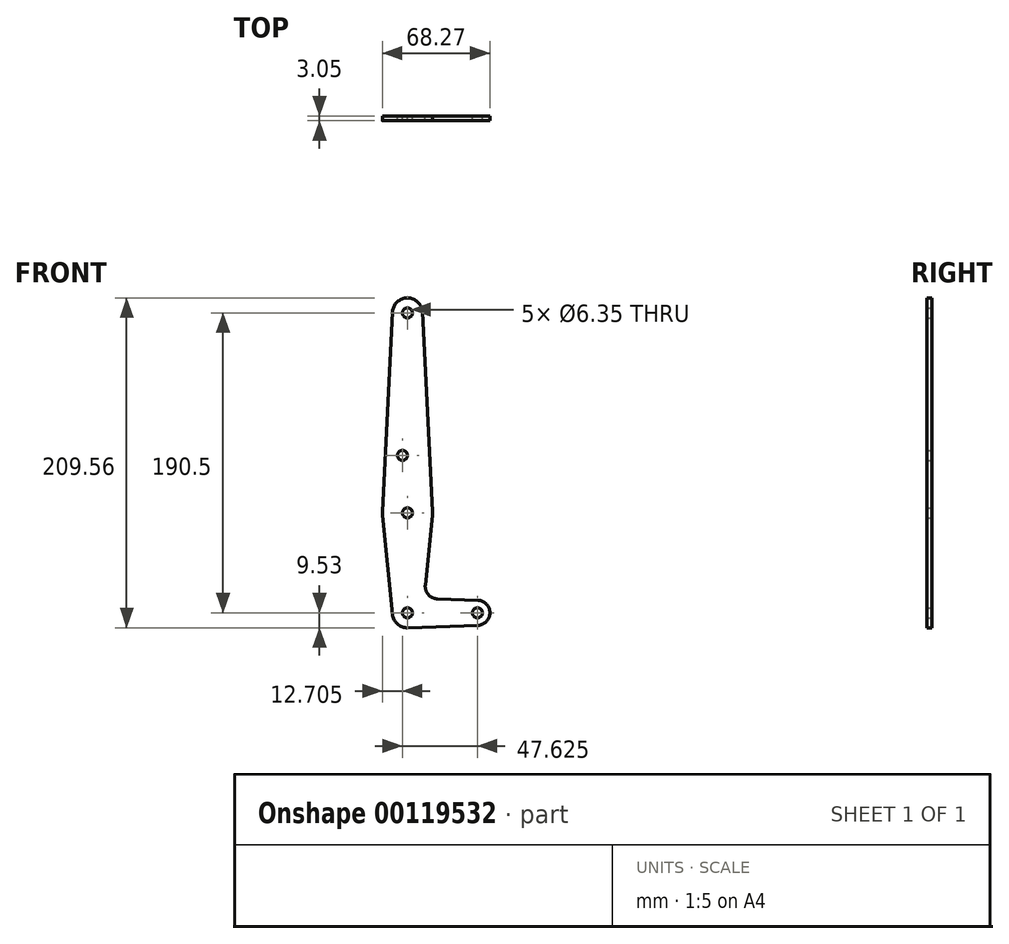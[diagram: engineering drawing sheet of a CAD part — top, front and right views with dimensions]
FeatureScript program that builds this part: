
annotation { "Feature Type Name" : "Feature", "Feature Type Description" : "" }
export const myFeature = defineFeature(function(context is Context, id is Id, definition is map)
    precondition{}
    {
        {
            var Q0;
            Q0=qCreatedBy(makeId("Front.planeOp"),FACE);
            var sketch = newSketch(context, id + "F0", { "sketchPlane" : qUnion([Q0])});
            skCircle(sketch, "E0", {"center": v(0, 0) * mm, "radius": 15.88 * mm});
            skCircle(sketch, "E1", {"center": v(0, 127) * mm, "radius": 9.53 * mm});
            skCircle(sketch, "E2", {"center": v(0, -63.5) * mm, "radius": 9.53 * mm});
            skCircle(sketch, "E3", {"center": v(44.45, -63.5) * mm, "radius": 7.94 * mm});
            skLineSegment(sketch, "E4", {"start": v(0, 127) * mm, "end": v(0, -63.5) * mm, "construction": true});
            skLineSegment(sketch, "E5", {"start": v(0, -63.5) * mm, "end": v(44.45, -63.5) * mm, "construction": true});
            skLineSegment(sketch, "E6", {"start": v(-15.8, -1.59) * mm, "end": v(-9.48, -64.45) * mm});
            skLineSegment(sketch, "E7", {"start": v(15.8, -1.59) * mm, "end": v(11.34, -45.9) * mm});
            skLineSegment(sketch, "E8", {"start": v(-9.51, 127.48) * mm, "end": v(-15.86, 0.8) * mm});
            skLineSegment(sketch, "E9", {"start": v(9.51, 127.48) * mm, "end": v(15.86, 0.8) * mm});
            skLineSegment(sketch, "E10", {"start": v(18.97, -54.65) * mm, "end": v(44.73, -55.57) * mm});
            skLineSegment(sketch, "E11", {"start": v(0.34, -73.02) * mm, "end": v(44.73, -71.43) * mm});
            skCircle(sketch, "E12", {"center": v(0, 127) * mm, "radius": 3.18 * mm});
            skCircle(sketch, "E13", {"center": v(0, 0) * mm, "radius": 3.18 * mm});
            skCircle(sketch, "E14", {"center": v(0, -63.5) * mm, "radius": 3.18 * mm});
            skCircle(sketch, "E15", {"center": v(44.45, -63.5) * mm, "radius": 3.18 * mm});
            skCircle(sketch, "E16", {"center": v(-3.17, 36.53) * mm, "radius": 3.18 * mm});
            skArc(sketch, "E17.filletArc", {"start": v(11.34, -45.9) * mm, "mid": v(13.26, -51.93) * mm, "end": v(18.97, -54.65) * mm});
            skSolve(sketch);
        }
        {
            var Q0;
            Q0=makeQuery(id+"F0.imprint","IMPRINT",FACE,{"disambiguationData":[TD([[makeQuery(id+"F0.imprint","IMPRINT",EDGE,{"derivedFrom":sQuery(id+"F0.wireOp",EDGE,"E12")}),-1.0]])]});
            var Q1;
            {var subQ0=sQuery(id+"F0.wireOp",EDGE,"E6");Q1=makeQuery(id+"F0.imprint","IMPRINT",FACE,{"disambiguationData":[TD([[makeQuery(id+"F0.imprint","IMPRINT",EDGE,{"derivedFrom":subQ0}),1.0]])]});}
            var Q2;
            Q2=makeQuery(id+"F0.imprint","IMPRINT",FACE,{"disambiguationData":[TD([[makeQuery(id+"F0.imprint","IMPRINT",EDGE,{"derivedFrom":sQuery(id+"F0.wireOp",EDGE,"E15")}),-1.0]])]});
            var Q3;
            Q3=makeQuery(id+"F0.imprint","IMPRINT",FACE,{"disambiguationData":[TD([[makeQuery(id+"F0.imprint","IMPRINT",EDGE,{"derivedFrom":sQuery(id+"F0.wireOp",EDGE,"E14")}),-1.0]])]});
            var Q4;
            {var subQ1=sQuery(id+"F0.wireOp",EDGE,"E8");Q4=makeQuery(id+"F0.imprint","IMPRINT",FACE,{"disambiguationData":[TD([[makeQuery(id+"F0.imprint","IMPRINT",EDGE,{"derivedFrom":subQ1}),1.0]])]});}
            var Q5;
            Q5=makeQuery(id+"F0.imprint","IMPRINT",FACE,{"disambiguationData":[TD([[makeQuery(id+"F0.imprint","IMPRINT",EDGE,{"derivedFrom":sQuery(id+"F0.wireOp",EDGE,"E13")}),-1.0]])]});
            extrude(context, id + "F1", {"entities" : qUnion([Q0, Q1, Q2, Q3, Q4, Q5]), "depth" : 3.05 * mm});
        }
    });
